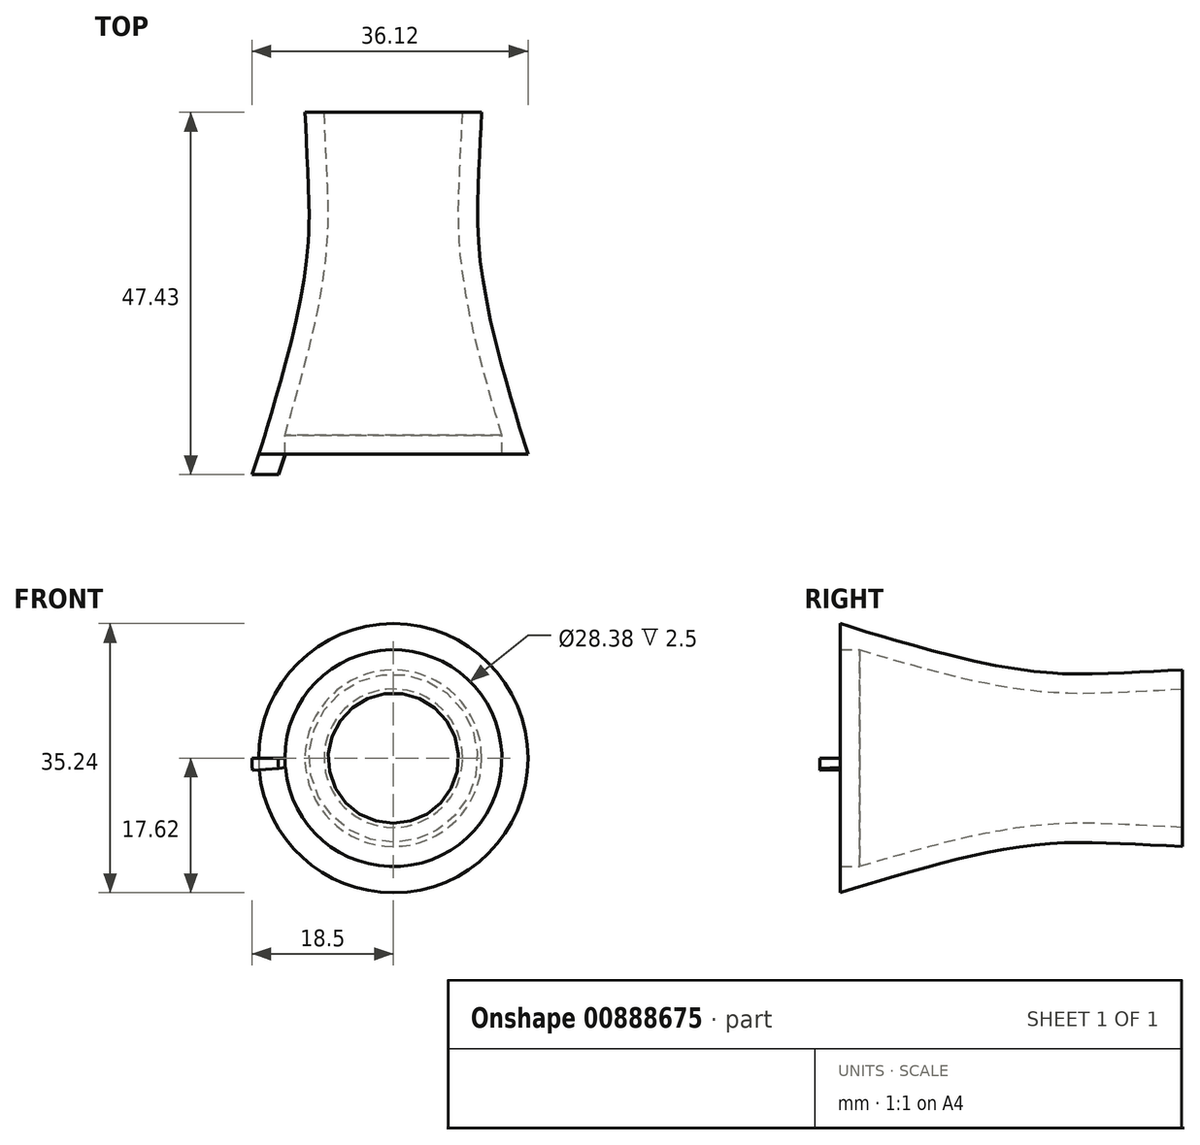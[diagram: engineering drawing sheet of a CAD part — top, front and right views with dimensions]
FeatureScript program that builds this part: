
annotation { "Feature Type Name" : "Feature", "Feature Type Description" : "" }
export const myFeature = defineFeature(function(context is Context, id is Id, definition is map)
    precondition{}
    {
        {
            var Q0;
            Q0=qCreatedBy(makeId("Top.planeOp"),FACE);
            var sketch = newSketch(context, id + "F0", { "sketchPlane" : qUnion([Q0])});
            skLineSegment(sketch, "E0", {"start": v(57.74, 87.36) * mm, "end": v(80.86, 87.36) * mm});
            skLineSegment(sketch, "E1", {"start": v(86.92, 42.63) * mm, "end": v(69.3, 42.63) * mm});
            skLineSegment(sketch, "E2", {"start": v(69.3, 42.63) * mm, "end": v(69.3, 87.36) * mm});
            skFitSpline(sketch, "E3", {"points": [v(80.86, 87.36) * mm, v(80.53, 80.4) * mm, v(80.32, 74.68) * mm, v(80.57, 68.91) * mm, v(81.68, 61.75) * mm, v(83.28, 55.02) * mm, v(85.27, 47.92) * mm, v(86.92, 42.63) * mm], "startDerivative": vector(-2.33, -48.11) * mm, "endDerivative": vector(15.52, -45.38) * mm});
            skSolve(sketch);
        }
        {
            var Q0;
            Q0=makeQuery(id+"F0.imprint","IMPRINT",FACE,{"disambiguationData":[TD([[makeQuery(id+"F0.imprint","IMPRINT",EDGE,{"derivedFrom":sQuery(id+"F0.wireOp",EDGE,"E1")}),-1.0]])]});
            var Q1;
            Q1=sQuery(id+"F0.wireOp",EDGE,"E2");
            revolve(context, id + "F1", {"surfaceOperationType" : NewSurfaceOperationType.NEW, "entities" : qUnion([Q0]), "axis" : qUnion([Q1]), "revolveType" : RevolveType.FULL});
        }
        {
            var Q0;
            Q0=makeQuery(id+"F1.opRevolve","SWEPT_FACE",FACE,{"disambiguationData":[OSD([sQuery(id+"F0.wireOp",EDGE,"E0")])]});
            shell(context, id + "F2", {"entities" : qUnion([Q0]), "thickness" : 2.5 * mm});
        }
        {
            var Q0;
            Q0=makeQuery(id+"F2.opShell","OFFSET_FACE",FACE,{"disambiguationData":[OSD([sQuery(id+"F0.wireOp",EDGE,"E1")])]});
            var sketch = newSketch(context, id + "F3", { "sketchPlane" : qUnion([Q0])});
            skCircle(sketch, "E4.0.0", {"center": v(-69.3, 0) * mm, "radius": 14.2 * mm});
            skSolve(sketch);
        }
        {
            var Q0;
            Q0 = qSketchRegion(id + "F3", true);
            extrude(context, id + "F4", {"entities" : qUnion([Q0]), "operationType" : NewBodyOperationType.REMOVE, "endBound" : BoundingType.THROUGH_ALL, "oppositeDirection" : true, "depth" : 25 * mm, "offsetDistance" : 25 * mm});
        }
        {
            var Q0;
            Q0=qCreatedBy(makeId("Top.planeOp"),FACE);
            var sketch = newSketch(context, id + "F5", { "sketchPlane" : qUnion([Q0])});
            skLineSegment(sketch, "E5", {"start": v(51.68, 42.63) * mm, "end": v(50.8, 39.93) * mm});
            skLineSegment(sketch, "E6", {"start": v(51.68, 42.63) * mm, "end": v(55.1, 42.63) * mm});
            skLineSegment(sketch, "E7", {"start": v(55.1, 42.63) * mm, "end": v(54.23, 39.93) * mm});
            skLineSegment(sketch, "E8", {"start": v(54.23, 39.93) * mm, "end": v(50.8, 39.93) * mm});
            skSolve(sketch);
        }
        {
            var Q0;
            Q0=makeQuery(id+"F5.imprint","IMPRINT",FACE,{"disambiguationData":[TD([[makeQuery(id+"F5.imprint","IMPRINT",EDGE,{"derivedFrom":sQuery(id+"F5.wireOp",EDGE,"E5")}),1.0]])]});
            var Q1;
            Q1=makeQuery(id+"F1.opRevolve","SWEPT_EDGE",EDGE,{"disambiguationData":[OSD([sQuery(id+"F0.wireOp",EDGE,"E0"),sQuery(id+"F0.wireOp",EDGE,"E3")])]});
            revolve(context, id + "F6", {"operationType" : NewBodyOperationType.ADD, "surfaceOperationType" : NewSurfaceOperationType.NEW, "entities" : qUnion([Q0]), "axis" : qUnion([Q1]), "revolveType" : RevolveType.ONE_DIRECTION, "angle" : 5 * degree});
        }
    });
